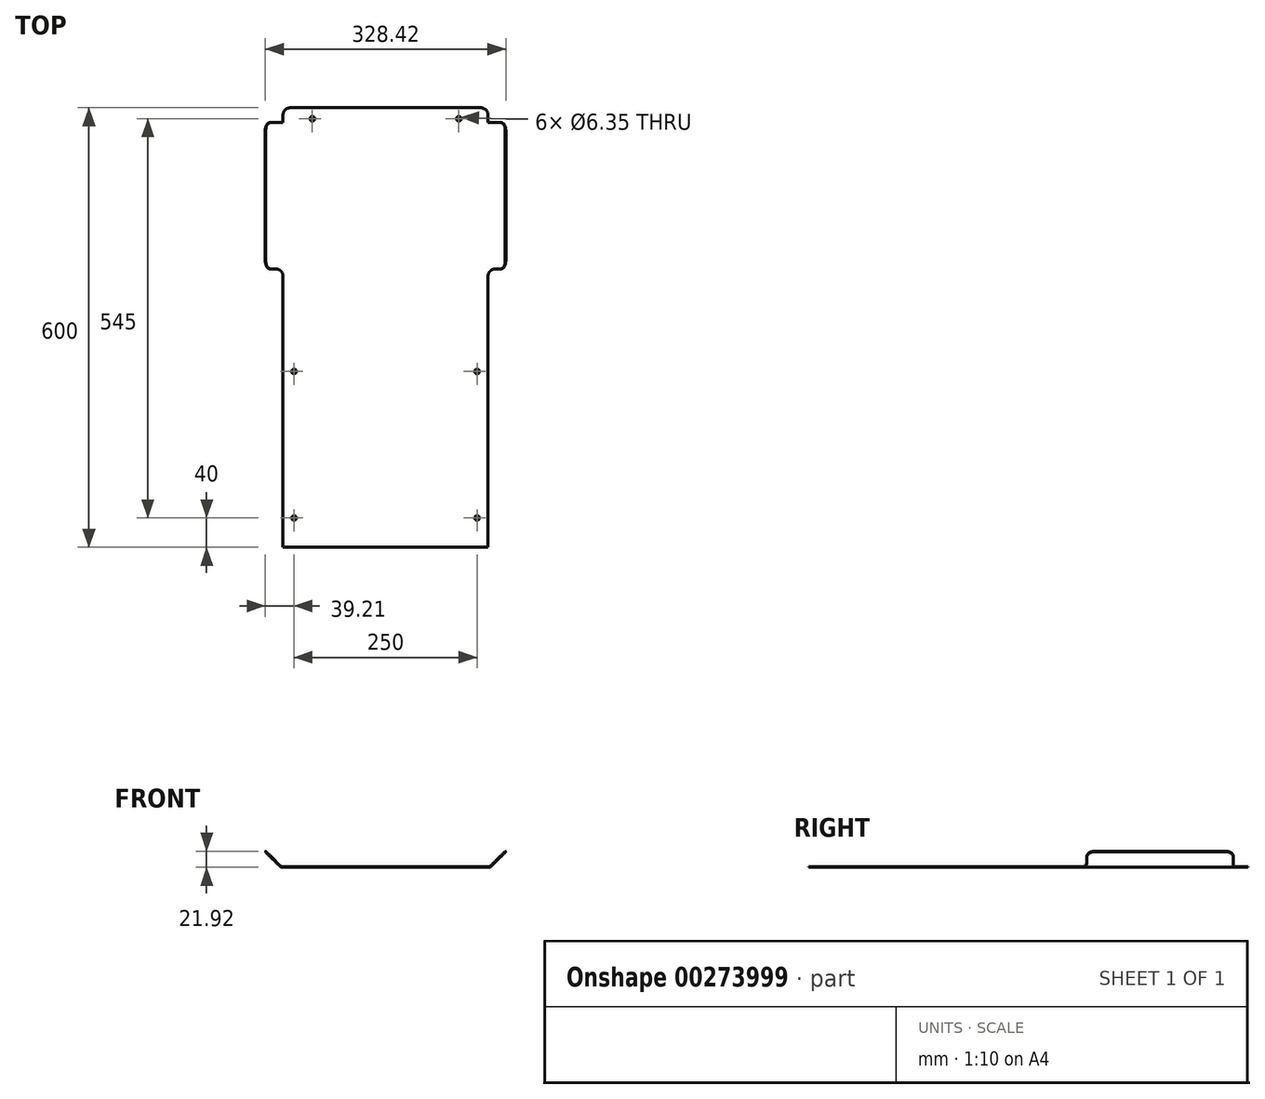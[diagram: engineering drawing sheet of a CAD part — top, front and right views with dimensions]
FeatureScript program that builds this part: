
annotation { "Feature Type Name" : "Feature", "Feature Type Description" : "" }
export const myFeature = defineFeature(function(context is Context, id is Id, definition is map)
    precondition{}
    {
        {
            var Q0;
            Q0=qCreatedBy(makeId("Top.planeOp"),FACE);
            var sketch = newSketch(context, id + "F0", { "sketchPlane" : qUnion([Q0])});
            skLineSegment(sketch, "E0.bottom", {"start": v(140, -300) * mm, "end": v(-140, -300) * mm});
            skLineSegment(sketch, "E0.top", {"start": v(140, 300) * mm, "end": v(-140, 300) * mm});
            skLineSegment(sketch, "E0.left", {"start": v(140, -300) * mm, "end": v(140, 300) * mm});
            skLineSegment(sketch, "E0.right", {"start": v(-140, -300) * mm, "end": v(-140, 300) * mm});
            skPoint(sketch, "E0.middle", {"position": v(0, 0) * mm});
            skSolve(sketch);
        }
        {
            var Q0;
            Q0=qSketchRegion(id+"F0",true);
            extrude(context, id + "F1", {"entities" : qUnion([Q0]), "depth" : 1 * mm});
        }
        {
            var Q0;
            Q0=makeQuery(id+"F1.opExtrude","SWEPT_FACE",FACE,{"disambiguationData":[OSD([sQuery(id+"F0.wireOp",EDGE,"E0.top")])]});
            cPlane(context, id + "F2", {"entities" : qUnion([Q0]), "cplaneType" : CPlaneType.OFFSET, "offset" : 20 * mm, "oppositeDirection" : true, "width" : 150 * mm, "height" : 150 * mm});
        }
        {
            var Q0;
            Q0=qCreatedBy(id+"F2.planeOp",FACE);
            var sketch = newSketch(context, id + "F3", { "sketchPlane" : qUnion([Q0])});
            skLineSegment(sketch, "E1", {"start": v(-140, 1) * mm, "end": v(-140, 0) * mm});
            skLineSegment(sketch, "E2", {"start": v(-140, 0) * mm, "end": v(-140.93, 0) * mm});
            skLineSegment(sketch, "E3", {"start": v(-144.46, 1.46) * mm, "end": v(-164.21, 21.21) * mm});
            skLineSegment(sketch, "E4", {"start": v(-164.21, 21.21) * mm, "end": v(-163.5, 21.92) * mm});
            skLineSegment(sketch, "E5", {"start": v(-163.5, 21.92) * mm, "end": v(-144.05, 2.46) * mm});
            skLineSegment(sketch, "E6", {"start": v(-140.51, 1) * mm, "end": v(-140, 1) * mm});
            skPoint(sketch, "E7.visualSharp", {"position": v(-143, 0) * mm});
            skArc(sketch, "E7.filletArc", {"start": v(-144.46, 1.46) * mm, "mid": v(-142.84, 0.38) * mm, "end": v(-140.93, 0) * mm});
            skPoint(sketch, "E8.visualSharp", {"position": v(-142.59, 1) * mm});
            skArc(sketch, "E8.filletArc", {"start": v(-144.05, 2.46) * mm, "mid": v(-142.43, 1.38) * mm, "end": v(-140.51, 1) * mm});
            skSolve(sketch);
        }
        {
            var Q0;
            Q0=qSketchRegion(id+"F3",true);
            extrude(context, id + "F4", {"entities" : qUnion([Q0]), "oppositeDirection" : true, "depth" : 200 * mm});
        }
        {
            var Q0;
            Q0=makeQuery(id+"F4.opExtrude","SWEPT_BODY",BODY,{"disambiguationData":[OSD([sQuery(id+"F3.wireOp",EDGE,"E1"),sQuery(id+"F3.wireOp",EDGE,"E2"),sQuery(id+"F3.wireOp",EDGE,"E3"),sQuery(id+"F3.wireOp",EDGE,"E4"),sQuery(id+"F3.wireOp",EDGE,"E5"),sQuery(id+"F3.wireOp",EDGE,"E6"),sQuery(id+"F3.wireOp",EDGE,"E7.filletArc"),sQuery(id+"F3.wireOp",EDGE,"E8.filletArc")])]});
            var Q1;
            Q1=qCreatedBy(makeId("Right.planeOp"),FACE);
            mirror(context, id + "F5", {"operationType" : NewBodyOperationType.ADD, "entities" : qUnion([Q0]), "mirrorPlane" : qUnion([Q1])});
        }
        {
            var Q0;
            Q0=makeQuery(id+"F1.opExtrude","SWEPT_EDGE",EDGE,{"disambiguationData":[OSD([sQuery(id+"F0.wireOp",EDGE,"E0.top"),sQuery(id+"F0.wireOp",EDGE,"E0.left")])]});
            var Q1;
            Q1=makeQuery(id+"F4.opExtrude","CAP_EDGE",EDGE,{"disambiguationData":[OSD([sQuery(id+"F3.wireOp",EDGE,"E1")])],"isStart":true});
            var Q2;
            Q2=makeQuery(id+"F4.opExtrude","CAP_EDGE",EDGE,{"disambiguationData":[OSD([sQuery(id+"F3.wireOp",EDGE,"E4")])],"isStart":true});
            var Q3;
            Q3=makeQuery(id+"F4.opExtrude","CAP_EDGE",EDGE,{"disambiguationData":[OSD([sQuery(id+"F3.wireOp",EDGE,"E4")])],"isStart":false});
            var Q4;
            Q4=makeQuery(id+"F4.opExtrude","CAP_EDGE",EDGE,{"disambiguationData":[OSD([sQuery(id+"F3.wireOp",EDGE,"E1")])],"isStart":false});
            var Q5;
            Q5=makeQuery(id+"F5.opPattern","COPY",EDGE,{"derivedFrom":makeQuery(id+"F4.opExtrude","CAP_EDGE",EDGE,{"disambiguationData":[OSD([sQuery(id+"F3.wireOp",EDGE,"E1")])],"isStart":false}),"instanceName":"1"});
            var Q6;
            Q6=makeQuery(id+"F5.opPattern","COPY",EDGE,{"derivedFrom":makeQuery(id+"F4.opExtrude","CAP_EDGE",EDGE,{"disambiguationData":[OSD([sQuery(id+"F3.wireOp",EDGE,"E4")])],"isStart":false}),"instanceName":"1"});
            var Q7;
            Q7=makeQuery(id+"F5.opPattern","COPY",EDGE,{"derivedFrom":makeQuery(id+"F4.opExtrude","CAP_EDGE",EDGE,{"disambiguationData":[OSD([sQuery(id+"F3.wireOp",EDGE,"E4")])],"isStart":true}),"instanceName":"1"});
            var Q8;
            Q8=makeQuery(id+"F5.opPattern","COPY",EDGE,{"derivedFrom":makeQuery(id+"F4.opExtrude","CAP_EDGE",EDGE,{"disambiguationData":[OSD([sQuery(id+"F3.wireOp",EDGE,"E1")])],"isStart":true}),"instanceName":"1"});
            var Q9;
            Q9=makeQuery(id+"F1.opExtrude","SWEPT_EDGE",EDGE,{"disambiguationData":[OSD([sQuery(id+"F0.wireOp",EDGE,"E0.top"),sQuery(id+"F0.wireOp",EDGE,"E0.right")])]});
            fillet(context, id + "F6", {"entities" : qUnion([Q0, Q1, Q2, Q3, Q4, Q5, Q6, Q7, Q8, Q9]), "radius" : 10 * mm, "tangentPropagation" : true, "allowEdgeOverflow" : false});
        }
        {
            var Q0;
            {var subQ0=makeQuery(id+"F4.opExtrude","SWEPT_FACE",FACE,{"disambiguationData":[OSD([sQuery(id+"F3.wireOp",EDGE,"E6")])]});Q0=makeQuery(id+"F5.boolean.opBoolean","MERGE",FACE,{"derivedFrom":[makeQuery(id+"F1.opExtrude","CAP_FACE",FACE,{"disambiguationData":[OSD([sQuery(id+"F0.wireOp",EDGE,"E0.bottom"),sQuery(id+"F0.wireOp",EDGE,"E0.top"),sQuery(id+"F0.wireOp",EDGE,"E0.left"),sQuery(id+"F0.wireOp",EDGE,"E0.right")])],"isStart":false}),subQ0,makeQuery(id+"F5.opPattern","COPY",FACE,{"derivedFrom":subQ0,"instanceName":"1"})]});}
            var sketch = newSketch(context, id + "F7", { "sketchPlane" : qUnion([Q0])});
            skCircle(sketch, "E9", {"center": v(-125, -260) * mm, "radius": 3.17 * mm});
            skCircle(sketch, "E10", {"center": v(-125, -60) * mm, "radius": 3.17 * mm});
            skCircle(sketch, "E11", {"center": v(125, -260) * mm, "radius": 3.17 * mm});
            skCircle(sketch, "E12", {"center": v(125, -60) * mm, "radius": 3.17 * mm});
            skCircle(sketch, "E13", {"center": v(-100, 285) * mm, "radius": 3.17 * mm});
            skCircle(sketch, "E14", {"center": v(100, 285) * mm, "radius": 3.17 * mm});
            skLineSegment(sketch, "E15", {"start": v(0, 0) * mm, "end": v(0, 394.67) * mm, "construction": true});
            skSolve(sketch);
        }
        {
            var Q0;
            Q0=qSketchRegion(id+"F7",true);
            extrude(context, id + "F8", {"entities" : qUnion([Q0]), "operationType" : NewBodyOperationType.REMOVE, "endBound" : BoundingType.THROUGH_ALL, "oppositeDirection" : true, "depth" : 25 * mm});
        }
    });
